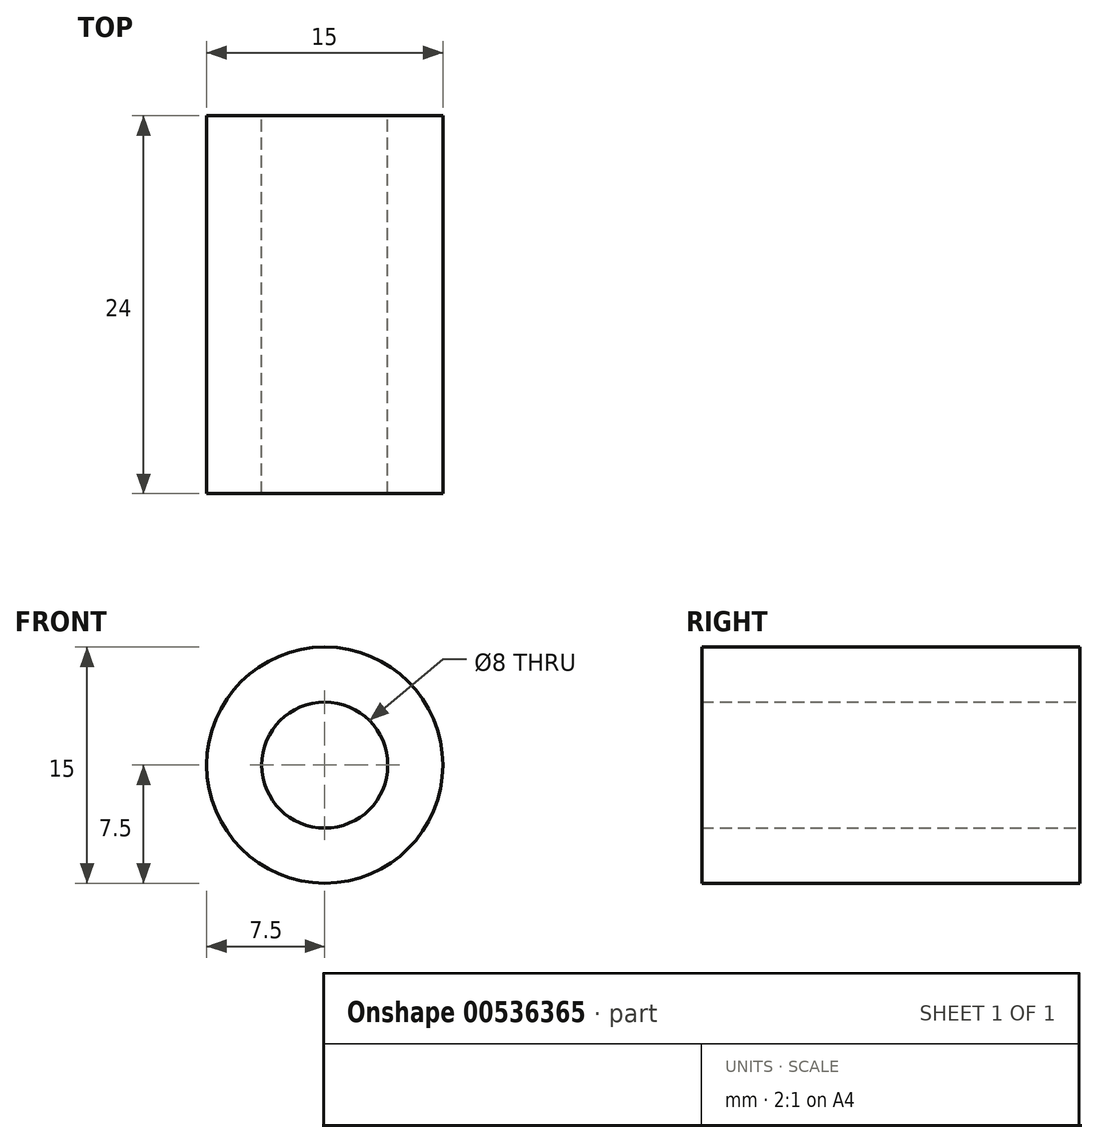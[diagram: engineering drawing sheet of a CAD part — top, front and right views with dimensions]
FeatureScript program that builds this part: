
annotation { "Feature Type Name" : "Feature", "Feature Type Description" : "" }
export const myFeature = defineFeature(function(context is Context, id is Id, definition is map)
    precondition{}
    {
        {
            var Q0;
            Q0=qCreatedBy(makeId("Front.planeOp"),FACE);
            var sketch = newSketch(context, id + "F0", { "sketchPlane" : qUnion([Q0])});
            skCircle(sketch, "E0", {"center": v(0, 0) * mm, "radius": 7.5 * mm});
            skCircle(sketch, "E1", {"center": v(0, 0) * mm, "radius": 4 * mm});
            skSolve(sketch);
        }
        {
            var Q0;
            Q0=makeQuery(id+"F0.imprint","IMPRINT",FACE,{"disambiguationData":[TD([[makeQuery(id+"F0.imprint","IMPRINT",EDGE,{"derivedFrom":sQuery(id+"F0.wireOp",EDGE,"E0")}),1.0]])]});
            extrude(context, id + "F1", {"entities" : qUnion([Q0]), "depth" : 24 * mm, "offsetDistance" : 25 * mm});
        }
    });
